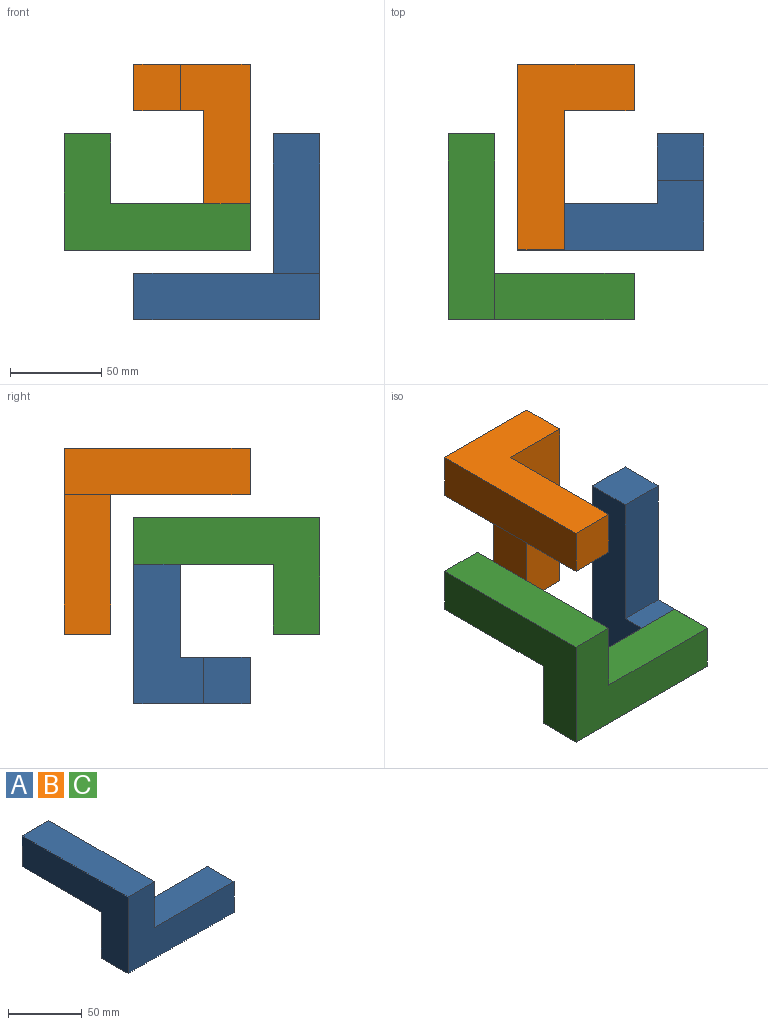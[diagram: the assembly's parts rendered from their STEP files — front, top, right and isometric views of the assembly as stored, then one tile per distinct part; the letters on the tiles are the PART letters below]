
ASSEMBLY  parts=3 mates=2
PART A: 10 faces, bbox 101.6x101.6x63.5 mm
  f0: plane 101.6x38.1mm, normal (0,1,0), area 2903.2mm2, adj f1,f2,f3,f4,f5,f8
  f1: plane 101.6x63.5mm, normal (-1,0,0), area 3548.4mm2, adj f0,f2,f6,f7,f8,f9
  f2: plane 101.6x25.4mm, normal (0,0,-1), area 2580.6mm2, adj f0,f1,f3,f7
  f3: plane 25.4x25.4mm, normal (1,0,0), area 645.2mm2, adj f0,f2,f4,f7
  f4: plane 76.2x25.4mm, normal (0,0,1), area 1935.5mm2, adj f0,f3,f5,f7
  f5: plane 101.6x38.1mm, normal (1,0,0), area 2903.2mm2, adj f0,f4,f6,f7,f8,f9
  f6: plane 101.6x25.4mm, normal (0,0,1), area 2580.6mm2, adj f1,f5,f7,f9
  f7: plane 101.6x63.5mm, normal (0,-1,0), area 3548.4mm2, adj f1,f2,f3,f4,f5,f6
  f8: plane 76.2x25.4mm, normal (0,0,-1), area 1935.5mm2, adj f0,f1,f5,f9
  f9: plane 25.4x25.4mm, normal (0,1,0), area 645.2mm2, adj f1,f5,f6,f8
PART B: same geometry as A
PART C: same geometry as A
PLACE A rot(axis=(0.58,-0.58,0.58),120deg) t=(146.55,101.21,-30.6)mm
PLACE B rot(axis=(-0.58,0.58,-0.58),120deg) t=(44.95,139.31,109.1)mm
PLACE C t=(6.85,-0.39,7.5)mm fixed
MATE planar A.f2 <-> C.f9  axis (0,1,0) through (133.85,101.21,20.2)mm
MATE planar A.f3 <-> C.f6  axis (0,0,1) through (133.85,75.81,71)mm
